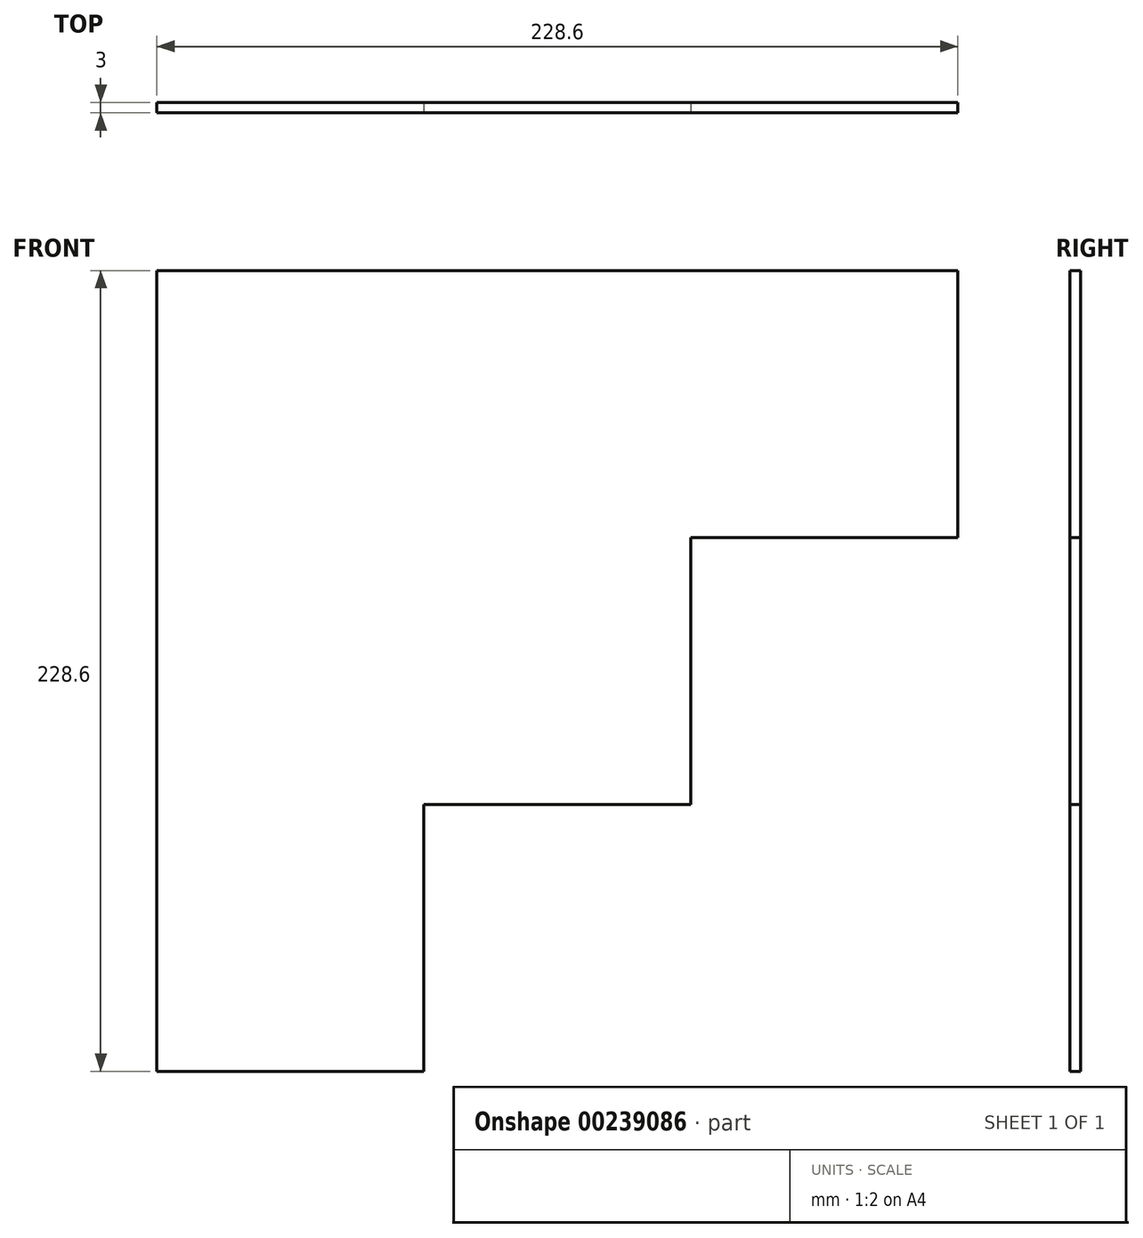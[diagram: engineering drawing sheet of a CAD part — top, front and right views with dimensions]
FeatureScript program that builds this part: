
annotation { "Feature Type Name" : "Feature", "Feature Type Description" : "" }
export const myFeature = defineFeature(function(context is Context, id is Id, definition is map)
    precondition{}
    {
        {
            assignVariable(context, id + "F0", {"name" : "v", "anyValue" : 3});
        }
        {
            var Q0;
            Q0=qCreatedBy(makeId("Front.planeOp"),FACE);
            var sketch = newSketch(context, id + "F1", { "sketchPlane" : qUnion([Q0])});
            skLineSegment(sketch, "E0.bottom", {"start": v(-114.3, 114.3) * mm, "end": v(114.3, 114.3) * mm});
            skLineSegment(sketch, "E0.top", {"start": v(-114.3, -114.3) * mm, "end": v(114.3, -114.3) * mm});
            skLineSegment(sketch, "E0.left", {"start": v(-114.3, 114.3) * mm, "end": v(-114.3, -114.3) * mm});
            skLineSegment(sketch, "E0.right", {"start": v(114.3, 114.3) * mm, "end": v(114.3, -114.3) * mm});
            skPoint(sketch, "E0.middle", {"position": v(0, 0) * mm});
            skSolve(sketch);
        }
        {
            var Q0;
            Q0 = qSketchRegion(id + "F1", true);
            extrude(context, id + "F2", {"entities" : qUnion([Q0]), "depth" : (getVariable(context, 'v')) * mm});
        }
        {
            var Q0;
            Q0=makeQuery(id+"F2.opExtrude","CAP_FACE",FACE,{"disambiguationData":[OSD([sQuery(id+"F1.wireOp",EDGE,"E0.bottom"),sQuery(id+"F1.wireOp",EDGE,"E0.top"),sQuery(id+"F1.wireOp",EDGE,"E0.left"),sQuery(id+"F1.wireOp",EDGE,"E0.right")])],"isStart":false});
            var sketch = newSketch(context, id + "F3", { "sketchPlane" : qUnion([Q0])});
            skLineSegment(sketch, "E1.bottom", {"start": v(114.3, -114.3) * mm, "end": v(38.1, -114.3) * mm});
            skLineSegment(sketch, "E1.top", {"start": v(114.3, -38.1) * mm, "end": v(38.1, -38.1) * mm});
            skLineSegment(sketch, "E1.left", {"start": v(114.3, -114.3) * mm, "end": v(114.3, -38.1) * mm});
            skLineSegment(sketch, "E1.right", {"start": v(38.1, -114.3) * mm, "end": v(38.1, -38.1) * mm});
            skLineSegment(sketch, "E2.top", {"start": v(114.3, 38.1) * mm, "end": v(38.1, 38.1) * mm});
            skLineSegment(sketch, "E2.left", {"start": v(114.3, -38.1) * mm, "end": v(114.3, 38.1) * mm});
            skLineSegment(sketch, "E2.right", {"start": v(38.1, -38.1) * mm, "end": v(38.1, 38.1) * mm});
            skLineSegment(sketch, "E3.bottom", {"start": v(38.1, -114.3) * mm, "end": v(-38.1, -114.3) * mm});
            skLineSegment(sketch, "E3.top", {"start": v(38.1, -38.1) * mm, "end": v(-38.1, -38.1) * mm});
            skLineSegment(sketch, "E3.right", {"start": v(-38.1, -114.3) * mm, "end": v(-38.1, -38.1) * mm});
            skSolve(sketch);
        }
        {
            var Q0;
            Q0 = qSketchRegion(id + "F3", true);
            extrude(context, id + "F4", {"entities" : qUnion([Q0]), "operationType" : NewBodyOperationType.REMOVE, "endBound" : BoundingType.THROUGH_ALL, "oppositeDirection" : true, "depth" : 25.4 * mm});
        }
    });
